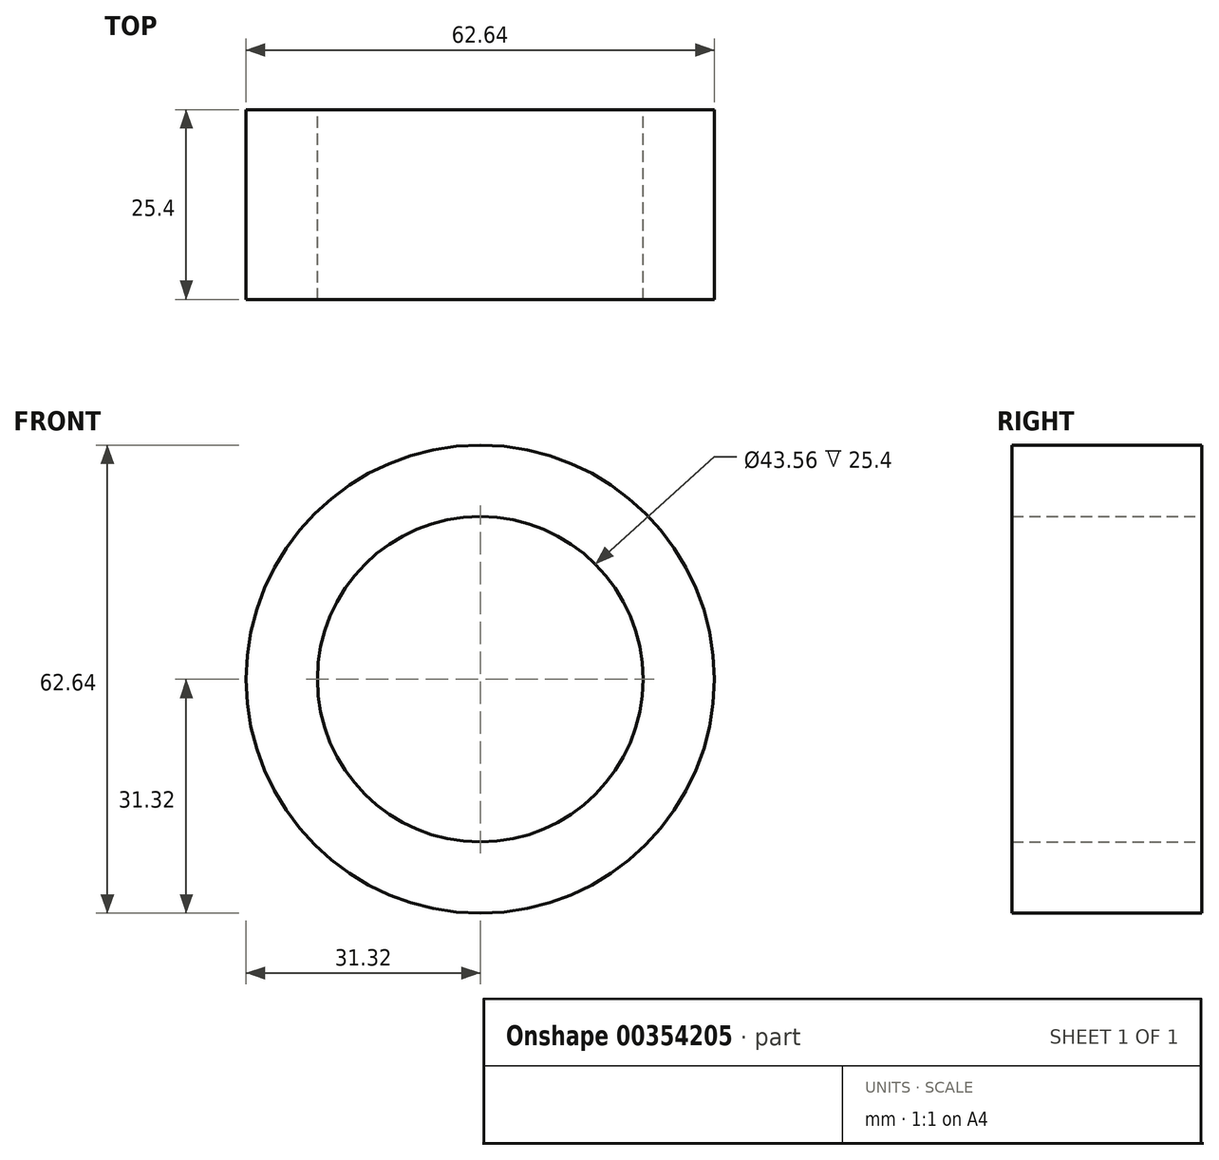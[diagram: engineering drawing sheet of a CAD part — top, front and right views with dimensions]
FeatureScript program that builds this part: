
annotation { "Feature Type Name" : "Feature", "Feature Type Description" : "" }
export const myFeature = defineFeature(function(context is Context, id is Id, definition is map)
    precondition{}
    {
        {
            var Q0;
            Q0=qCreatedBy(makeId("Front.planeOp"),FACE);
            var sketch = newSketch(context, id + "F0", { "sketchPlane" : qUnion([Q0])});
            skCircle(sketch, "E0", {"center": v(0, 0) * mm, "radius": 31.32 * mm});
            skCircle(sketch, "E1", {"center": v(0, 0) * mm, "radius": 21.78 * mm});
            skSolve(sketch);
        }
        {
            var Q0;
            Q0 = qSketchRegion(id + "F0", true);
            extrude(context, id + "F1", {"entities" : qUnion([Q0]), "depth" : 25.4 * mm});
        }
    });
